# Revit family: PRD_AR_ShwrFttngsPckg_MountingPlate_ACXX2023
name_source: partatom
category: Specialty Equipment
units: mm (PartAtom-declared; Revit-internal decimal feet)

## family parameters
Cut with Voids When Loaded = Yes
Enable Cutting in Views = Yes
Host = Face
Maintain Annotation Orientation = No
OmniClass Number = 23.45.05.14.99
OmniClass Title = Other Sanitary Washing Plumbing Fixtures
Part Type = Normal
Room Calculation Point = No
Round Connector Dimension = Use Diameter
Shared = No

## types (1)
- ACXX2023
    AdjustableTiltAngle = No
    AssetType = Fixed
    BIMObjectName = PRD_AR_ShowerFittingsPackage_MountingPlate_ACXX2023
    BodyMaterial = PRD_AR_StainlessSteel_Brushed
    CW Connection = Yes
    CWFU = 0
    Category = Pr_40_20_87_75, Shower fittings package
    Default Elevation = 1219 mm
    Description = Mounting plate with connecting nozzles for shower head DN 15 for concealed mounting. Especially suitable for facilities at risk of vandalism. Stainless steel plate 190 x 245 x 2 mm for invisible mounting via threaded rods, up to a wall thickness of 50 to 500 mm, with connecting nozzle with pre-fitted flow regulator 9.0 l/min for KWC shower head DN 15 (required separately).
    Export Type to IFC As = IfcSanitaryTerminalType
    Features = Stainless steel plate 190 x 245 x 2 mm for invisiblemounting via threaded rods, up to a wall thickness of 50 to 500 mm
    HW Connection = Yes
    HWFU = 0
    IfcExportAs = IfcSanitaryTerminalType
    IfcExportType = USERDEFINED
    Manufacturer = KWC Group Management AG
    ManufacturerName = KWC Group Management AG
    ManufacturerURL = www.kwc-professional.com
    Material = Stainless steel
    Model = ACXX2023
    ModelNumber = 2030068175
    ModelReference = ACXX2023
    NBSDescription = Shower fittings package
    NBSReference = 45-35-70/330
    Name = Mounting plate ACXX2023
    NominalDepth = 2 mm  [stored 0.00656168 ft]
    NominalHeight = 245 mm  [stored 0.803806 ft]
    NominalLength = 245 mm  [stored 0.803806 ft]
    NominalWidth = 190 mm
    ProductInformation = http://pim.kwc.com
    Size = 15
    Status = New
    Type = Shower head
    Type IFC Predefined Type = USERDEFINED
    TypeOfShowerHead = Jet shower head
    URL = www.kwc-professional.com
    Uniclass2015Code = Pr_40_20_87_75
    Uniclass2015Title = Shower fittings package
    Uniclass2015Version = Products v1.36
    Vent Connection = Yes
    Version = 1
    WFU = 0
    Waste Connection = Yes

note: [stored X ft] marks values corroborated as IEEE doubles in the binary element streams (Revit-internal decimal feet)

## geometry (parser evidence)
native form markers: Sweep x6
no freeform markers — native parametric forms only
